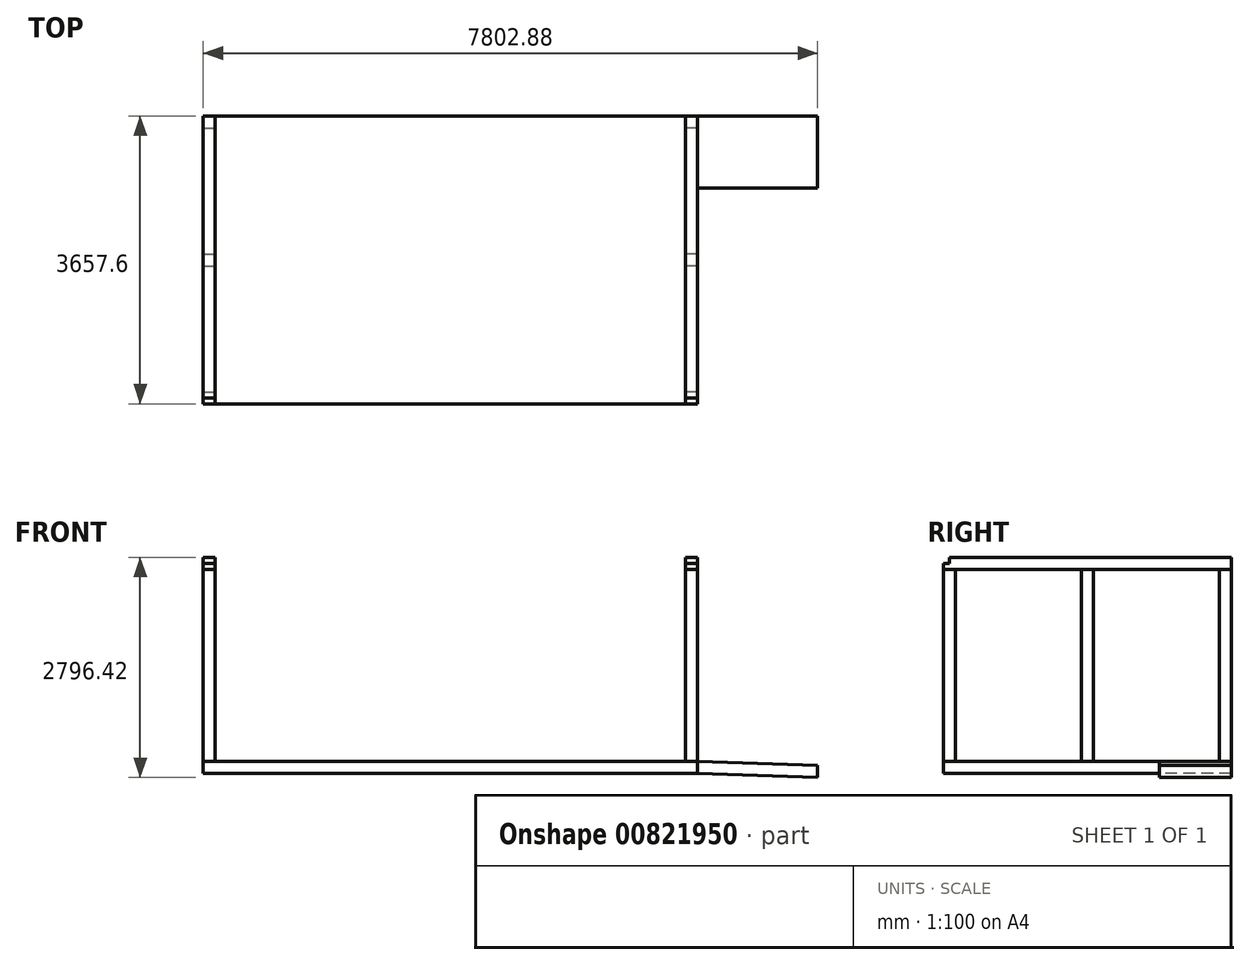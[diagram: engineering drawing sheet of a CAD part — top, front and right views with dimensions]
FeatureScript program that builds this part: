
annotation { "Feature Type Name" : "Feature", "Feature Type Description" : "" }
export const myFeature = defineFeature(function(context is Context, id is Id, definition is map)
    precondition{}
    {
        {
            var Q0;
            Q0=qCreatedBy(makeId("Top.planeOp"),FACE);
            var sketch = newSketch(context, id + "F0", { "sketchPlane" : qUnion([Q0])});
            skLineSegment(sketch, "E0.bottom", {"start": v(-3139.44, 1828.8) * mm, "end": v(3139.44, 1828.8) * mm});
            skLineSegment(sketch, "E0.top", {"start": v(-3139.44, -1828.8) * mm, "end": v(3139.44, -1828.8) * mm});
            skLineSegment(sketch, "E0.left", {"start": v(-3139.44, 1828.8) * mm, "end": v(-3139.44, -1828.8) * mm});
            skLineSegment(sketch, "E0.right", {"start": v(3139.44, 1828.8) * mm, "end": v(3139.44, -1828.8) * mm});
            skPoint(sketch, "E0.middle", {"position": v(0, 0) * mm});
            skSolve(sketch);
        }
        {
            var Q0;
            Q0 = qSketchRegion(id + "F0", true);
            extrude(context, id + "F1", {"entities" : qUnion([Q0]), "depth" : 152.4 * mm, "offsetDistance" : 25.4 * mm});
        }
        {
            var Q0;
            Q0=makeQuery(id+"F1.opExtrude","CAP_FACE",FACE,{"disambiguationData":[OSD([sQuery(id+"F0.wireOp",EDGE,"E0.bottom"),sQuery(id+"F0.wireOp",EDGE,"E0.top"),sQuery(id+"F0.wireOp",EDGE,"E0.left"),sQuery(id+"F0.wireOp",EDGE,"E0.right")])],"isStart":false});
            var sketch = newSketch(context, id + "F2", { "sketchPlane" : qUnion([Q0])});
            skLineSegment(sketch, "E1.bottom", {"start": v(-3139.44, -1828.8) * mm, "end": v(-2987.04, -1828.8) * mm});
            skLineSegment(sketch, "E1.top", {"start": v(-3139.44, -1676.4) * mm, "end": v(-2987.04, -1676.4) * mm});
            skLineSegment(sketch, "E1.left", {"start": v(-3139.44, -1828.8) * mm, "end": v(-3139.44, -1676.4) * mm});
            skLineSegment(sketch, "E1.right", {"start": v(-2987.04, -1828.8) * mm, "end": v(-2987.04, -1676.4) * mm});
            skLineSegment(sketch, "E2.bottom", {"start": v(-3139.44, 1828.8) * mm, "end": v(-2987.04, 1828.8) * mm});
            skLineSegment(sketch, "E2.top", {"start": v(-3139.44, 1676.4) * mm, "end": v(-2987.04, 1676.4) * mm});
            skLineSegment(sketch, "E2.left", {"start": v(-3139.44, 1828.8) * mm, "end": v(-3139.44, 1676.4) * mm});
            skLineSegment(sketch, "E2.right", {"start": v(-2987.04, 1828.8) * mm, "end": v(-2987.04, 1676.4) * mm});
            skLineSegment(sketch, "E3.bottom", {"start": v(3139.44, 1828.8) * mm, "end": v(2987.04, 1828.8) * mm});
            skLineSegment(sketch, "E3.top", {"start": v(3139.44, 1676.4) * mm, "end": v(2987.04, 1676.4) * mm});
            skLineSegment(sketch, "E3.left", {"start": v(3139.44, 1828.8) * mm, "end": v(3139.44, 1676.4) * mm});
            skLineSegment(sketch, "E3.right", {"start": v(2987.04, 1828.8) * mm, "end": v(2987.04, 1676.4) * mm});
            skLineSegment(sketch, "E4.bottom", {"start": v(3139.44, -1828.8) * mm, "end": v(2987.04, -1828.8) * mm});
            skLineSegment(sketch, "E4.top", {"start": v(3139.44, -1676.4) * mm, "end": v(2987.04, -1676.4) * mm});
            skLineSegment(sketch, "E4.left", {"start": v(3139.44, -1828.8) * mm, "end": v(3139.44, -1676.4) * mm});
            skLineSegment(sketch, "E4.right", {"start": v(2987.04, -1828.8) * mm, "end": v(2987.04, -1676.4) * mm});
            skSolve(sketch);
        }
        {
            var Q0;
            Q0 = qSketchRegion(id + "F2", true);
            extrude(context, id + "F3", {"entities" : qUnion([Q0]), "depth" : 2438.4 * mm, "offsetDistance" : 25.4 * mm});
        }
        {
            var Q0;
            Q0=makeQuery(id+"F1.opExtrude","CAP_FACE",FACE,{"disambiguationData":[OSD([sQuery(id+"F0.wireOp",EDGE,"E0.bottom"),sQuery(id+"F0.wireOp",EDGE,"E0.top"),sQuery(id+"F0.wireOp",EDGE,"E0.left"),sQuery(id+"F0.wireOp",EDGE,"E0.right")])],"isStart":false});
            var sketch = newSketch(context, id + "F4", { "sketchPlane" : qUnion([Q0])});
            skLineSegment(sketch, "E5.bottom", {"start": v(-3139.44, 76.2) * mm, "end": v(-2987.04, 76.2) * mm});
            skLineSegment(sketch, "E5.top", {"start": v(-3139.44, -76.2) * mm, "end": v(-2987.04, -76.2) * mm});
            skLineSegment(sketch, "E5.left", {"start": v(-3139.44, 76.2) * mm, "end": v(-3139.44, -76.2) * mm});
            skLineSegment(sketch, "E5.right", {"start": v(-2987.04, 76.2) * mm, "end": v(-2987.04, -76.2) * mm});
            skLineSegment(sketch, "E6", {"start": v(0, 0) * mm, "end": v(-2987.04, 0) * mm, "construction": true});
            skLineSegment(sketch, "E7", {"start": v(0, 0) * mm, "end": v(0, 1828.8) * mm, "construction": true});
            skLineSegment(sketch, "E8.MirrorCS", {"start": v(3139.44, 76.2) * mm, "end": v(2987.04, 76.2) * mm});
            skLineSegment(sketch, "E9.MirrorCS", {"start": v(3139.44, 76.2) * mm, "end": v(3139.44, -76.2) * mm});
            skLineSegment(sketch, "E10.MirrorCS", {"start": v(3139.44, -76.2) * mm, "end": v(2987.04, -76.2) * mm});
            skLineSegment(sketch, "E11.MirrorCS", {"start": v(2987.04, 76.2) * mm, "end": v(2987.04, -76.2) * mm});
            skSolve(sketch);
        }
        {
            var Q0;
            Q0 = qSketchRegion(id + "F4", true);
            extrude(context, id + "F5", {"entities" : qUnion([Q0]), "depth" : 2438.4 * mm, "offsetDistance" : 25.4 * mm});
        }
        {
            var Q0;
            Q0=makeQuery(id+"F1.opExtrude","SWEPT_FACE",FACE,{"disambiguationData":[OSD([sQuery(id+"F0.wireOp",EDGE,"E0.bottom")])]});
            var sketch = newSketch(context, id + "F6", { "sketchPlane" : qUnion([Q0])});
            skLineSegment(sketch, "E12", {"start": v(-3139.44, 152.4) * mm, "end": v(-4663.44, 99.18) * mm});
            skLineSegment(sketch, "E13", {"start": v(-4663.44, 99.18) * mm, "end": v(-4663.44, -53.22) * mm});
            skLineSegment(sketch, "E14", {"start": v(-4663.44, -53.22) * mm, "end": v(-3139.44, 0) * mm});
            skLineSegment(sketch, "E15", {"start": v(-3139.44, 0) * mm, "end": v(-3139.44, 152.4) * mm});
            skSolve(sketch);
        }
        {
            var Q0;
            Q0 = qSketchRegion(id + "F6", true);
            extrude(context, id + "F7", {"entities" : qUnion([Q0]), "operationType" : NewBodyOperationType.ADD, "oppositeDirection" : true, "depth" : 914.4 * mm, "offsetDistance" : 25.4 * mm});
        }
        {
            var Q0;
            Q0=makeQuery(id+"F3.opExtrude","SWEPT_FACE",FACE,{"disambiguationData":[OSD([sQuery(id+"F2.wireOp",EDGE,"E1.bottom")])]});
            var sketch = newSketch(context, id + "F8", { "sketchPlane" : qUnion([Q0])});
            skLineSegment(sketch, "E16.bottom", {"start": v(-3139.44, 2590.8) * mm, "end": v(-2987.04, 2590.8) * mm});
            skLineSegment(sketch, "E16.top", {"start": v(-3139.44, 2743.2) * mm, "end": v(-2987.04, 2743.2) * mm});
            skLineSegment(sketch, "E16.left", {"start": v(-3139.44, 2590.8) * mm, "end": v(-3139.44, 2743.2) * mm});
            skLineSegment(sketch, "E16.right", {"start": v(-2987.04, 2590.8) * mm, "end": v(-2987.04, 2743.2) * mm});
            skSolve(sketch);
        }
        {
            var Q0;
            Q0 = qSketchRegion(id + "F8", true);
            extrude(context, id + "F9", {"entities" : qUnion([Q0]), "oppositeDirection" : true, "depth" : 3657.6 * mm, "offsetDistance" : 25.4 * mm});
        }
        {
            var Q0;
            Q0=makeQuery(id+"F9.opExtrude","CAP_FACE",FACE,{"disambiguationData":[OSD([sQuery(id+"F8.wireOp",EDGE,"E16.bottom"),sQuery(id+"F8.wireOp",EDGE,"E16.top"),sQuery(id+"F8.wireOp",EDGE,"E16.left"),sQuery(id+"F8.wireOp",EDGE,"E16.right")])],"isStart":true});
            var sketch = newSketch(context, id + "F10", { "sketchPlane" : qUnion([Q0])});
            skLineSegment(sketch, "E17.bottom", {"start": v(-3139.44, 2743.2) * mm, "end": v(-2987.04, 2743.2) * mm});
            skLineSegment(sketch, "E17.top", {"start": v(-3139.44, 2667) * mm, "end": v(-2987.04, 2667) * mm});
            skLineSegment(sketch, "E17.left", {"start": v(-3139.44, 2743.2) * mm, "end": v(-3139.44, 2667) * mm});
            skLineSegment(sketch, "E17.right", {"start": v(-2987.04, 2743.2) * mm, "end": v(-2987.04, 2667) * mm});
            skSolve(sketch);
        }
        {
            var Q0;
            Q0 = qSketchRegion(id + "F10", true);
            extrude(context, id + "F11", {"entities" : qUnion([Q0]), "operationType" : NewBodyOperationType.REMOVE, "oppositeDirection" : true, "depth" : 76.2 * mm, "offsetDistance" : 25.4 * mm});
        }
        {
            var Q0;
            Q0=makeQuery(id+"F9.opExtrude","SWEPT_BODY",BODY,{"disambiguationData":[OSD([sQuery(id+"F8.wireOp",EDGE,"E16.bottom"),sQuery(id+"F8.wireOp",EDGE,"E16.top"),sQuery(id+"F8.wireOp",EDGE,"E16.left"),sQuery(id+"F8.wireOp",EDGE,"E16.right")])]});
            var Q1;
            Q1=qCreatedBy(makeId("Right.planeOp"),FACE);
            mirror(context, id + "F12", {"entities" : qUnion([Q0]), "mirrorPlane" : qUnion([Q1])});
        }
    });
